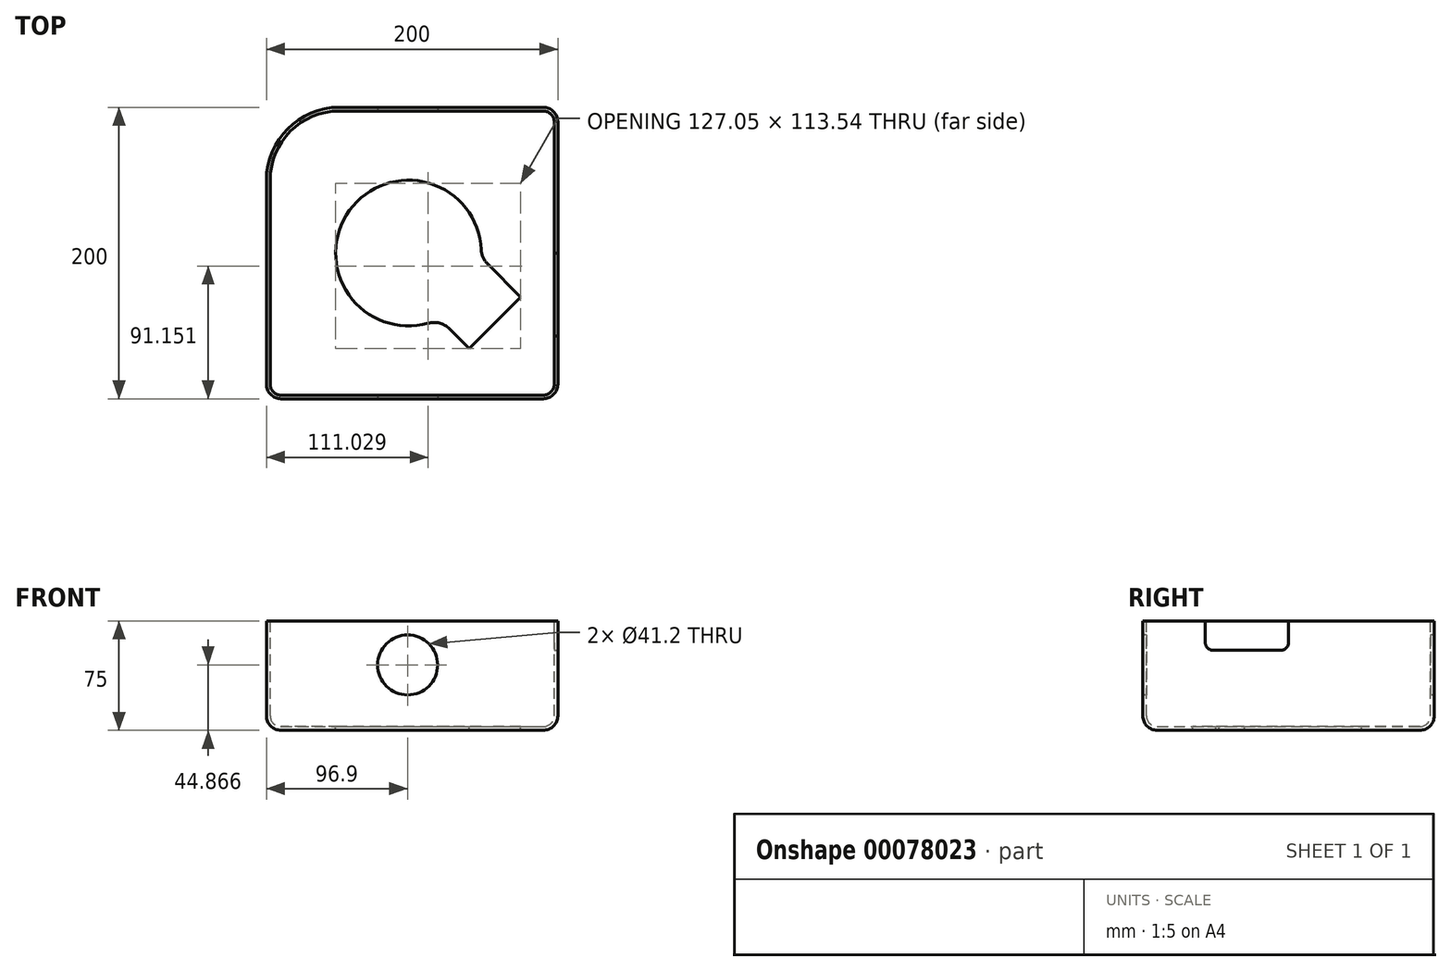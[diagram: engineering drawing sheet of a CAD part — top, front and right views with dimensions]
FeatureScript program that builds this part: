
annotation { "Feature Type Name" : "Feature", "Feature Type Description" : "" }
export const myFeature = defineFeature(function(context is Context, id is Id, definition is map)
    precondition{}
    {
        {
            var Q0;
            Q0=qCreatedBy(makeId("Top.planeOp"),FACE);
            var sketch = newSketch(context, id + "F0", { "sketchPlane" : qUnion([Q0])});
            skLineSegment(sketch, "E0.bottom", {"start": v(-96.9, -100) * mm, "end": v(103.1, -100) * mm});
            skLineSegment(sketch, "E0.top", {"start": v(-96.9, 100) * mm, "end": v(103.1, 100) * mm});
            skLineSegment(sketch, "E0.left", {"start": v(-96.9, -100) * mm, "end": v(-96.9, 100) * mm});
            skLineSegment(sketch, "E0.right", {"start": v(103.1, -100) * mm, "end": v(103.1, 100) * mm});
            skSolve(sketch);
        }
        {
            var Q0;
            Q0=makeQuery(id+"F0.imprint","IMPRINT",FACE,{"disambiguationData":[TD([[makeQuery(id+"F0.imprint","IMPRINT",EDGE,{"derivedFrom":sQuery(id+"F0.wireOp",EDGE,"E0.bottom")}),1.0]])]});
            extrude(context, id + "F1", {"entities" : qUnion([Q0]), "depth" : 75 * mm});
        }
        {
            var Q0;
            Q0=makeQuery(id+"F1.opExtrude","SWEPT_EDGE",EDGE,{"disambiguationData":[OSD([sQuery(id+"F0.wireOp",EDGE,"E0.bottom"),sQuery(id+"F0.wireOp",EDGE,"E0.left")])]});
            var Q1;
            Q1=makeQuery(id+"F1.opExtrude","SWEPT_EDGE",EDGE,{"disambiguationData":[OSD([sQuery(id+"F0.wireOp",EDGE,"E0.bottom"),sQuery(id+"F0.wireOp",EDGE,"E0.right")])]});
            var Q2;
            Q2=makeQuery(id+"F1.opExtrude","SWEPT_EDGE",EDGE,{"disambiguationData":[OSD([sQuery(id+"F0.wireOp",EDGE,"E0.top"),sQuery(id+"F0.wireOp",EDGE,"E0.right")])]});
            fillet(context, id + "F2", {"entities" : qUnion([Q0, Q1, Q2]), "radius" : 10 * mm, "tangentPropagation" : true, "allowEdgeOverflow" : false});
        }
        {
            var Q0;
            Q0=makeQuery(id+"F1.opExtrude","SWEPT_EDGE",EDGE,{"disambiguationData":[OSD([sQuery(id+"F0.wireOp",EDGE,"E0.top"),sQuery(id+"F0.wireOp",EDGE,"E0.left")])]});
            fillet(context, id + "F3", {"entities" : qUnion([Q0]), "radius" : 50 * mm, "tangentPropagation" : true, "allowEdgeOverflow" : false});
        }
        {
            var Q0;
            Q0=makeQuery(id+"F1.opExtrude","CAP_EDGE",EDGE,{"disambiguationData":[OSD([sQuery(id+"F0.wireOp",EDGE,"E0.top")])],"isStart":true});
            fillet(context, id + "F4", {"entities" : qUnion([Q0]), "radius" : 10 * mm, "tangentPropagation" : true, "allowEdgeOverflow" : false});
        }
        {
            var Q0;
            Q0=makeQuery(id+"F1.opExtrude","CAP_FACE",FACE,{"disambiguationData":[OSD([sQuery(id+"F0.wireOp",EDGE,"E0.bottom"),sQuery(id+"F0.wireOp",EDGE,"E0.top"),sQuery(id+"F0.wireOp",EDGE,"E0.left"),sQuery(id+"F0.wireOp",EDGE,"E0.right")])],"isStart":false});
            shell(context, id + "F5", {"entities" : qUnion([Q0]), "thickness" : 2.5 * mm});
        }
        {
            var Q0;
            Q0=makeQuery(id+"F1.opExtrude","SWEPT_FACE",FACE,{"disambiguationData":[OSD([sQuery(id+"F0.wireOp",EDGE,"E0.bottom")])]});
            var sketch = newSketch(context, id + "F6", { "sketchPlane" : qUnion([Q0])});
            skCircle(sketch, "E1", {"center": v(0, 44.87) * mm, "radius": 20.6 * mm});
            skSolve(sketch);
        }
        {
            var Q0;
            Q0=makeQuery(id+"F6.imprint","IMPRINT",FACE,{"disambiguationData":[TD([[makeQuery(id+"F6.imprint","IMPRINT",EDGE,{"derivedFrom":sQuery(id+"F6.wireOp",EDGE,"E1")}),1.0]])]});
            extrude(context, id + "F7", {"entities" : qUnion([Q0]), "operationType" : NewBodyOperationType.REMOVE, "endBound" : BoundingType.THROUGH_ALL, "oppositeDirection" : true, "depth" : 25 * mm});
        }
        {
            var Q0;
            {var subQ0=sQuery(id+"F0.wireOp",EDGE,"E0.right");var subQ1=sQuery(id+"F0.wireOp",EDGE,"E0.left");var subQ2=sQuery(id+"F0.wireOp",EDGE,"E0.top");var subQ3=sQuery(id+"F0.wireOp",EDGE,"E0.bottom");Q0=makeQuery(id+"F5.opShell","OFFSET_FACE",FACE,{"disambiguationData":[OSD([subQ3,subQ2,subQ1,subQ0]),TDD([makeQuery(id+"F1.opExtrude","CAP_FACE",FACE,{"disambiguationData":[OSD([subQ3,subQ2,subQ1,subQ0])],"isStart":true})])]});}
            var sketch = newSketch(context, id + "F8", { "sketchPlane" : qUnion([Q0])});
            skArc(sketch, "E2", {"start": v(50.55, 2.36) * mm, "mid": v(-39.92, 29.28) * mm, "end": v(14.04, -48.16) * mm});
            skLineSegment(sketch, "E3", {"start": v(28.68, -52) * mm, "end": v(42.3, -65.62) * mm});
            skLineSegment(sketch, "E4", {"start": v(42.3, -65.62) * mm, "end": v(77.65, -30.27) * mm});
            skLineSegment(sketch, "E5", {"start": v(77.65, -30.27) * mm, "end": v(54.92, -7.54) * mm});
            skPoint(sketch, "E6.visualSharp", {"position": v(21.9, -45.23) * mm});
            skArc(sketch, "E6.filletArc", {"start": v(28.68, -52) * mm, "mid": v(21.88, -48.1) * mm, "end": v(14.04, -48.16) * mm});
            skPoint(sketch, "E7.visualSharp", {"position": v(50.5, -3.12) * mm});
            skArc(sketch, "E7.filletArc", {"start": v(50.55, 2.36) * mm, "mid": v(51.81, -3) * mm, "end": v(54.92, -7.54) * mm});
            skSolve(sketch);
        }
        {
            var Q0;
            Q0=makeQuery(id+"F8.imprint","IMPRINT",FACE,{"disambiguationData":[TD([[makeQuery(id+"F8.imprint","IMPRINT",EDGE,{"derivedFrom":sQuery(id+"F8.wireOp",EDGE,"E2")}),1.0]])]});
            var Q1;
            Q1=sQuery(id+"F8.wireOp",EDGE,"E2");
            extrude(context, id + "F9", {"entities" : qUnion([Q0]), "operationType" : NewBodyOperationType.REMOVE, "surfaceEntities" : qUnion([Q1]), "endBound" : BoundingType.UP_TO_NEXT, "oppositeDirection" : true, "depth" : 25 * mm});
        }
        {
            var Q0;
            Q0=makeQuery(id+"F1.opExtrude","SWEPT_FACE",FACE,{"disambiguationData":[OSD([sQuery(id+"F0.wireOp",EDGE,"E0.right")])]});
            var sketch = newSketch(context, id + "F10", { "sketchPlane" : qUnion([Q0])});
            skLineSegment(sketch, "E8", {"start": v(-52.07, 55) * mm, "end": v(-5, 55) * mm});
            skLineSegment(sketch, "E9", {"start": v(0, 60) * mm, "end": v(0, 75) * mm});
            skLineSegment(sketch, "E10", {"start": v(-57.07, 60) * mm, "end": v(-57.07, 75) * mm});
            skPoint(sketch, "E11.visualSharp", {"position": v(0, 55) * mm});
            skArc(sketch, "E11.filletArc", {"start": v(-5, 55) * mm, "mid": v(-1.46, 56.46) * mm, "end": v(0, 60) * mm});
            skPoint(sketch, "E12.visualSharp", {"position": v(-57.07, 55) * mm});
            skArc(sketch, "E12.filletArc", {"start": v(-57.07, 60) * mm, "mid": v(-55.6, 56.46) * mm, "end": v(-52.07, 55) * mm});
            skSolve(sketch);
        }
        {
            var Q0;
            Q0=makeQuery(id+"F10.imprint","IMPRINT",FACE,{"disambiguationData":[TD([[makeQuery(id+"F10.imprint","IMPRINT",EDGE,{"derivedFrom":sQuery(id+"F10.wireOp",EDGE,"E8")}),1.0]])]});
            extrude(context, id + "F11", {"entities" : qUnion([Q0]), "operationType" : NewBodyOperationType.REMOVE, "endBound" : BoundingType.UP_TO_NEXT, "oppositeDirection" : true, "depth" : 25 * mm});
        }
    });
